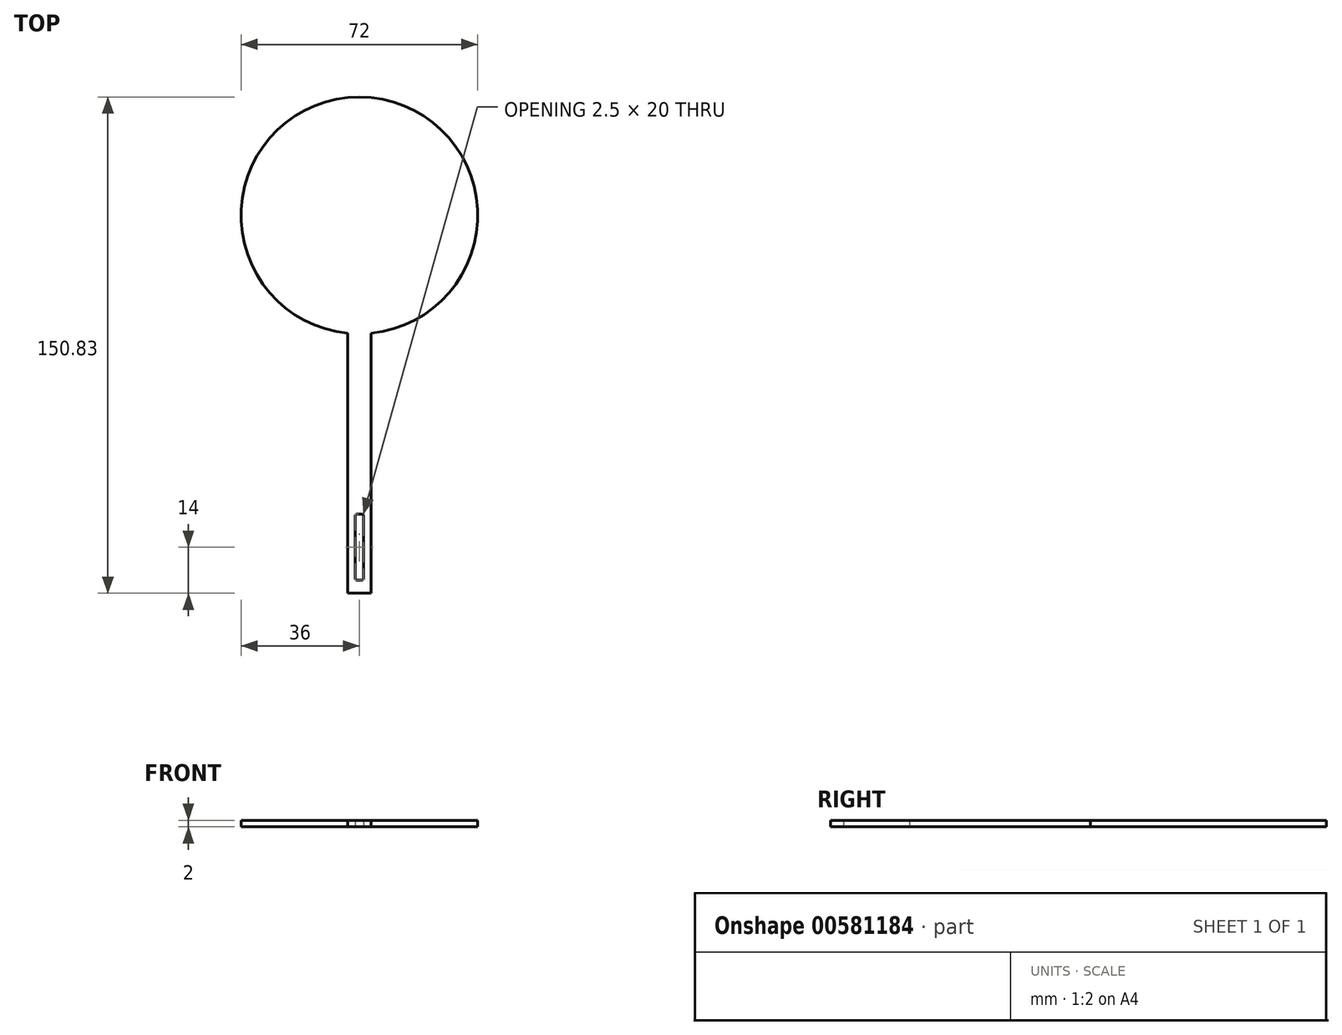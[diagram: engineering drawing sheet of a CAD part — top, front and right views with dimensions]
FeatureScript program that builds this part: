
annotation { "Feature Type Name" : "Feature", "Feature Type Description" : "" }
export const myFeature = defineFeature(function(context is Context, id is Id, definition is map)
    precondition{}
    {
        {
            var Q0;
            Q0=qCreatedBy(makeId("Top.planeOp"),FACE);
            var sketch = newSketch(context, id + "F0", { "sketchPlane" : qUnion([Q0])});
            skLineSegment(sketch, "E0.bottom", {"start": v(0, 0) * mm, "end": v(7, 0) * mm});
            skLineSegment(sketch, "E0.left", {"start": v(0, 0) * mm, "end": v(0, 79) * mm});
            skLineSegment(sketch, "E0.right", {"start": v(7, 0) * mm, "end": v(7, 79) * mm});
            skLineSegment(sketch, "E1.bottom", {"start": v(2.75, 24) * mm, "end": v(4.25, 24) * mm});
            skLineSegment(sketch, "E1.top", {"start": v(2.75, 4) * mm, "end": v(4.25, 4) * mm});
            skLineSegment(sketch, "E1.left", {"start": v(2.25, 23.5) * mm, "end": v(2.25, 4.5) * mm});
            skLineSegment(sketch, "E1.right", {"start": v(4.75, 23.5) * mm, "end": v(4.75, 4.5) * mm});
            skPoint(sketch, "E2.visualSharp", {"position": v(2.25, 24) * mm});
            skArc(sketch, "E2.filletArc", {"start": v(2.75, 24) * mm, "mid": v(2.4, 23.85) * mm, "end": v(2.25, 23.5) * mm});
            skPoint(sketch, "E3.visualSharp", {"position": v(4.75, 24) * mm});
            skArc(sketch, "E3.filletArc", {"start": v(4.75, 23.5) * mm, "mid": v(4.6, 23.85) * mm, "end": v(4.25, 24) * mm});
            skPoint(sketch, "E4.visualSharp", {"position": v(2.25, 4) * mm});
            skArc(sketch, "E4.filletArc", {"start": v(2.25, 4.5) * mm, "mid": v(2.4, 4.15) * mm, "end": v(2.75, 4) * mm});
            skPoint(sketch, "E5.visualSharp", {"position": v(4.75, 4) * mm});
            skArc(sketch, "E5.filletArc", {"start": v(4.25, 4) * mm, "mid": v(4.6, 4.15) * mm, "end": v(4.75, 4.5) * mm});
            skArc(sketch, "E6", {"start": v(7, 79) * mm, "mid": v(3.5, 150.83) * mm, "end": v(0, 79) * mm});
            skPoint(sketch, "E7.end.orphan", {"position": v(3.5, 0) * mm});
            skPoint(sketch, "E7.start.orphan", {"position": v(3.5, 4) * mm});
            skSolve(sketch);
        }
        {
            var Q0;
            Q0 = qSketchRegion(id + "F0", true);
            extrude(context, id + "F1", {"entities" : qUnion([Q0]), "depth" : 2 * mm, "offsetDistance" : 25.4 * mm});
        }
    });
